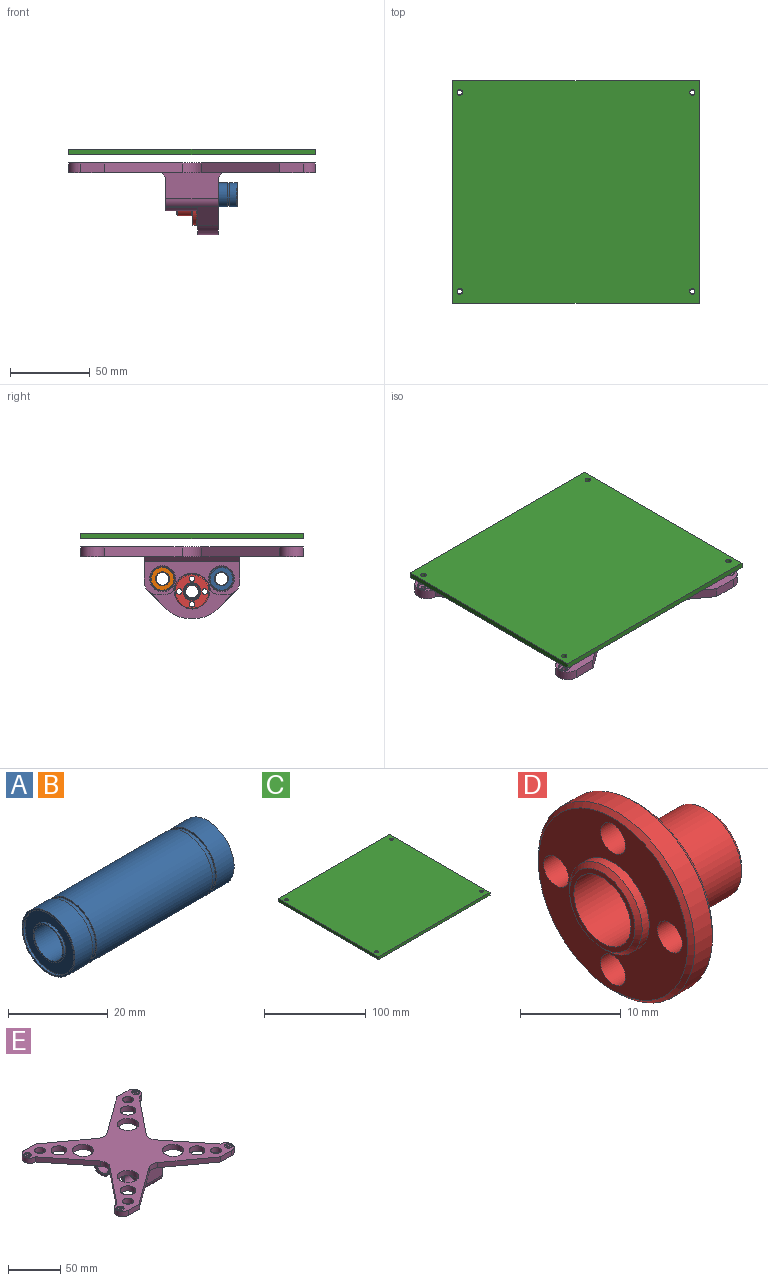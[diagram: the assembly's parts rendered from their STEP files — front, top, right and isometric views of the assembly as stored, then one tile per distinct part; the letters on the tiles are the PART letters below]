
ASSEMBLY  parts=5 mates=4
PART A: 20 faces, bbox 45x15x15 mm
  f0: plane 8.7x8.7mm, normal (-1,0,0), area 9.2mm2, adj f4,f17
  f1: plane 8.7x8.7mm, normal (1,0,0), area 9.2mm2, adj f4,f14
  f2: cylinder r=7.5mm len=32.8mm, axis (-1,0,0), area 1545.7mm2, adj f8,f11
  f3: cylinder r=7.5mm len=15mm, axis (-1,0,0), area 235.6mm2, adj f7,f9
  f4: cylinder r=4mm len=45mm, axis (-1,0,0), area 1131mm2, adj f0,f1
  f5: cylinder r=7.5mm len=15mm, axis (-1,0,0), area 235.6mm2, adj f6,f12
  f6: plane 15x15mm, normal (1,0,0), area 16.1mm2, adj f5,f15
  f7: plane 15x15mm, normal (-1,0,0), area 16.1mm2, adj f3,f18
  f8: plane 15x15mm, normal (-1,0,0), area 16.1mm2, adj f2,f10
  f9: plane 15x15mm, normal (1,0,0), area 16.1mm2, adj f3,f10
  f10: cylinder r=7.15mm len=14.3mm, axis (-1,0,0), area 49.4mm2, adj f8,f9
  f11: plane 15x15mm, normal (1,0,0), area 16.1mm2, adj f2,f13
  f12: plane 15x15mm, normal (-1,0,0), area 16.1mm2, adj f5,f13
  f13: cylinder r=7.15mm len=14.3mm, axis (1,0,0), area 49.4mm2, adj f11,f12
  f14: cylinder r=4.35mm len=8.7mm, axis (1,0,0), area 13.7mm2, adj f1,f16
  f15: cylinder r=7.15mm len=14.3mm, axis (1,0,0), area 22.5mm2, adj f6,f16
  f16: plane 14.3x14.3mm, normal (1,0,0), area 101.2mm2, adj f14,f15
  f17: cylinder r=4.35mm len=8.7mm, axis (-1,0,0), area 13.7mm2, adj f0,f19
  f18: cylinder r=7.15mm len=14.3mm, axis (-1,0,0), area 22.5mm2, adj f7,f19
  f19: plane 14.3x14.3mm, normal (-1,0,0), area 101.2mm2, adj f17,f18
PART B: same geometry as A
PART C: 10 faces, bbox 155x140x3.5 mm
  f0: plane 155x140mm, normal (0,0,1), area 21661.5mm2, adj f2,f3,f4,f5,f6,f7,f8,f9
  f1: plane 155x140mm, normal (0,0,-1), area 21661.5mm2, adj f2,f3,f4,f5,f6,f7,f8,f9
  f2: plane 140x3.5mm, normal (1,0,0), area 490mm2, adj f0,f1,f3,f5
  f3: plane 155x3.5mm, normal (0,1,0), area 542.5mm2, adj f0,f1,f2,f4
  f4: plane 140x3.5mm, normal (-1,0,0), area 490mm2, adj f0,f1,f3,f5
  f5: plane 155x3.5mm, normal (0,-1,0), area 542.5mm2, adj f0,f1,f2,f4
  f6: cylinder r=1.75mm len=3.5mm, axis (0,0,1), area 38.5mm2, adj f0,f1
  f7: cylinder r=1.75mm len=3.5mm, axis (0,0,1), area 38.5mm2, adj f0,f1
  f8: cylinder r=1.75mm len=3.5mm, axis (0,0,1), area 38.5mm2, adj f0,f1
  f9: cylinder r=1.75mm len=3.5mm, axis (0,0,1), area 38.5mm2, adj f0,f1
PART D: 17 faces, bbox 15x22x22 mm
  f0: cylinder r=11mm len=22mm, axis (-1,0,0), area 172.8mm2, adj f10,f11
  f1: plane 21x21mm, normal (1,0,0), area 209.4mm2, adj f8,f11,f13,f14,f15,f16
  f2: plane 21x21mm, normal (-1,0,0), area 226.2mm2, adj f6,f10,f13,f14,f15,f16
  f3: cylinder r=5.1mm len=10.2mm, axis (-1,0,0), area 288.4mm2, adj f8,f12
  f4: plane 9.2x9.2mm, normal (1,0,0), area 16.2mm2, adj f5,f12
  f5: cylinder r=4mm len=15mm, axis (1,0,0), area 377mm2, adj f4,f7
  f6: cylinder r=5.1mm len=10.2mm, axis (1,0,0), area 32mm2, adj f2,f9
  f7: plane 9.2x9.2mm, normal (-1,0,0), area 16.2mm2, adj f5,f9
  f8: cone r=5.1mm half-angle=45deg, axis (-1,0,0), area 23.8mm2, adj f1,f3
  f9: cone r=4.6mm half-angle=45deg, axis (1,0,0), area 21.5mm2, adj f6,f7
  f10: cone r=11mm half-angle=45deg, axis (1,0,0), area 47.8mm2, adj f0,f2
  f11: cone r=10.5mm half-angle=45deg, axis (-1,0,0), area 47.8mm2, adj f0,f1
  f12: cone r=4.6mm half-angle=45deg, axis (-1,0,0), area 21.5mm2, adj f3,f4
  f13: cylinder r=1.75mm len=3.5mm, axis (1,0,0), area 38.5mm2, adj f1,f2
  f14: cylinder r=1.75mm len=3.5mm, axis (1,0,0), area 38.5mm2, adj f1,f2
  f15: cylinder r=1.75mm len=3.5mm, axis (1,0,0), area 38.5mm2, adj f1,f2
  f16: cylinder r=1.75mm len=3.5mm, axis (1,0,0), area 38.5mm2, adj f1,f2
PART E: 83 faces, bbox 155x140x45 mm
  f0: plane 60x21.18mm, normal (-1,0,0), area 548.7mm2, adj f1,f2,f5,f6,f19,f20,f21,f25
  f1: plane 38.8x16.1mm, normal (0,-1,0), area 537.1mm2, adj f0,f3,f34,f35,f81,f82
  f2: plane 38.8x16.1mm, normal (0,1,0), area 537.1mm2, adj f0,f3,f33,f35,f81,f82
  f3: plane 60x36mm, normal (1,0,0), area 1172.9mm2, adj f1,f2,f4,f5,f6,f7,f8,f14
  f4: plane 12.8x3.43mm, normal (0,0,-1), area 43.9mm2, adj f3,f7,f8,f13
  f5: plane 32.8x12.09mm, normal (0,-0.71,-0.71), area 249.2mm2, adj f0,f3,f7,f13,f32,f34
  f6: plane 32.8x12.09mm, normal (0,0.71,-0.71), area 249.1mm2, adj f0,f3,f8,f13,f31,f33
  f7: cylinder r=20mm len=14.14mm, axis (1,0,0), area 201.1mm2, adj f3,f4,f5,f13
  f8: cylinder r=20mm len=14.14mm, axis (1,0,0), area 201.1mm2, adj f3,f4,f6,f13
  f9: cylinder r=7.68mm len=31.8mm, axis (1,0,0), area 1533.5mm2, adj f20,f23
  f10: cylinder r=5.4mm len=11.8mm, axis (1,0,0), area 400.4mm2, adj f18,f24
  f11: cylinder r=7.68mm len=31.8mm, axis (1,0,0), area 1533.5mm2, adj f21,f22
  f12: cylinder r=11mm len=21.11mm, axis (-1,0,0), area 551.3mm2, adj f13,f19,f29,f30
  f13: plane 53.76x28mm, normal (-1,0,0), area 608.4mm2, adj f4,f5,f6,f7,f8,f12,f14,f15
  f14: cylinder r=1.75mm len=12.8mm, axis (-1,0,0), area 140.7mm2, adj f3,f13
  f15: cylinder r=1.75mm len=12.8mm, axis (-1,0,0), area 140.7mm2, adj f3,f13
  f16: cylinder r=1.75mm len=12.8mm, axis (-1,0,0), area 140.7mm2, adj f3,f13
  f17: cylinder r=1.75mm len=12.8mm, axis (-1,0,0), area 140.7mm2, adj f3,f13
  f18: cone r=5.4mm half-angle=45deg, axis (-1,0,0), area 25.1mm2, adj f10,f13
  f19: cone r=11mm half-angle=45deg, axis (-1,0,0), area 22.4mm2, adj f0,f12,f29,f30
  f20: cone r=7.68mm half-angle=45deg, axis (-1,0,0), area 35.2mm2, adj f0,f9
  f21: cone r=7.68mm half-angle=45deg, axis (-1,0,0), area 35.2mm2, adj f0,f11
  f22: cone r=7.68mm half-angle=45deg, axis (1,0,0), area 35.2mm2, adj f3,f11
  f23: cone r=7.68mm half-angle=45deg, axis (1,0,0), area 35.2mm2, adj f3,f9
  f24: cone r=5.4mm half-angle=45deg, axis (1,0,0), area 25.1mm2, adj f3,f10
  f25: cylinder r=10.18mm len=20mm, axis (-1,0,0), area 89mm2, adj f0,f13,f26,f30
  f26: plane 20x3.03mm, normal (0,0,-1), area 60.6mm2, adj f0,f13,f25,f31
  f27: cylinder r=10.18mm len=20mm, axis (-1,0,0), area 85.3mm2, adj f0,f13,f28,f29
  f28: plane 20x3.21mm, normal (0,0,-1), area 64.2mm2, adj f0,f13,f27,f32
  f29: cylinder r=7mm len=20mm, axis (1,0,0), area 123.5mm2, adj f0,f12,f13,f19,f27
  f30: cylinder r=7mm len=20mm, axis (1,0,0), area 123.5mm2, adj f0,f12,f13,f19,f25
  f31: cylinder r=7mm len=20mm, axis (-1,0,0), area 110mm2, adj f0,f6,f13,f26
  f32: cylinder r=7mm len=20mm, axis (-1,0,0), area 110mm2, adj f0,f5,f13,f28
  f33: cylinder r=7mm len=32.8mm, axis (-1,0,0), area 180.3mm2, adj f0,f2,f3,f6
  f34: cylinder r=7mm len=32.8mm, axis (1,0,0), area 180.3mm2, adj f0,f1,f3,f5
  f35: plane 155x140mm, normal (0,0,-1), area 6124.2mm2, adj f1,f2,f37,f40,f43,f46,f48,f49
  f36: plane 7.5x7.5mm, normal (0,0,1), area 37.1mm2, adj f37,f38
  f37: cylinder r=1.5mm len=4.5mm, axis (0,0,1), area 42.4mm2, adj f35,f36
  f38: cylinder r=3.75mm len=7.5mm, axis (0,0,1), area 35.3mm2, adj f36,f79
  f39: plane 7.5x7.5mm, normal (0,0,1), area 37.1mm2, adj f40,f41
  f40: cylinder r=1.5mm len=4.5mm, axis (0,0,1), area 42.4mm2, adj f35,f39
  f41: cylinder r=3.75mm len=7.5mm, axis (0,0,1), area 35.3mm2, adj f39,f79
  f42: plane 7.5x7.5mm, normal (0,0,1), area 37.1mm2, adj f43,f44
  f43: cylinder r=1.5mm len=4.5mm, axis (0,0,1), area 42.4mm2, adj f35,f42
  f44: cylinder r=3.75mm len=7.5mm, axis (0,0,1), area 35.3mm2, adj f42,f79
  f45: plane 7.5x7.5mm, normal (0,0,1), area 37.1mm2, adj f46,f47
  f46: cylinder r=1.5mm len=4.5mm, axis (0,0,1), area 42.4mm2, adj f35,f45
  f47: cylinder r=3.75mm len=7.5mm, axis (0,0,1), area 35.3mm2, adj f45,f79
  f48: cylinder r=5mm len=10mm, axis (0,0,-1), area 188.5mm2, adj f35,f79
  f49: cylinder r=10mm len=20mm, axis (0,0,-1), area 377mm2, adj f35,f79
  f50: cylinder r=7.5mm len=15mm, axis (0,0,-1), area 282.7mm2, adj f35,f79
  f51: cylinder r=10mm len=20mm, axis (0,0,-1), area 377mm2, adj f35,f79
  f52: cylinder r=7.5mm len=15mm, axis (0,0,-1), area 282.7mm2, adj f35,f79
  f53: cylinder r=7.5mm len=15mm, axis (0,0,1), area 141.4mm2, adj f35,f54,f72,f79
  f54: plane 15x6mm, normal (0,-1,0), area 90mm2, adj f35,f53,f55,f79
  f55: plane 49.12x35.72mm, normal (0.59,-0.81,0), area 364.4mm2, adj f35,f54,f56,f79
  f56: cylinder r=10mm len=11.76mm, axis (0,0,1), area 75.5mm2, adj f35,f55,f57,f79
  f57: plane 49.12x35.72mm, normal (-0.59,-0.81,0), area 364.4mm2, adj f35,f56,f58,f79
  f58: plane 15x6mm, normal (0,-1,0), area 90mm2, adj f35,f57,f59,f79
  f59: cylinder r=7.5mm len=15mm, axis (0,0,1), area 141.4mm2, adj f35,f58,f60,f79
  f60: plane 48.75x39mm, normal (0.78,0.62,0), area 374.6mm2, adj f35,f59,f61,f79
  f61: cylinder r=10mm len=12.49mm, axis (0,0,1), area 81mm2, adj f35,f60,f62,f79
  f62: plane 48.75x39mm, normal (0.78,-0.62,0), area 374.6mm2, adj f35,f61,f63,f79
  f63: cylinder r=7.5mm len=15mm, axis (0,0,1), area 141.4mm2, adj f35,f62,f64,f79
  f64: plane 15x6mm, normal (0,1,0), area 90mm2, adj f35,f63,f65,f79
  f65: plane 49.12x35.72mm, normal (-0.59,0.81,0), area 364.4mm2, adj f35,f64,f66,f79
  f66: cylinder r=10mm len=11.76mm, axis (0,0,1), area 75.5mm2, adj f35,f65,f67,f79
  f67: plane 49.12x35.72mm, normal (0.59,0.81,0), area 364.4mm2, adj f35,f66,f68,f79
  f68: plane 15x6mm, normal (0,1,0), area 90mm2, adj f35,f67,f69,f79
  f69: cylinder r=7.5mm len=15mm, axis (0,0,1), area 141.4mm2, adj f35,f68,f70,f79
  f70: plane 48.75x39mm, normal (-0.78,-0.62,0), area 374.6mm2, adj f35,f69,f71,f79
  f71: cylinder r=10mm len=12.49mm, axis (0,0,1), area 81mm2, adj f35,f70,f72,f79
  f72: plane 48.75x39mm, normal (-0.78,0.62,0), area 374.6mm2, adj f35,f53,f71,f79
  f73: cylinder r=10mm len=20mm, axis (0,0,-1), area 377mm2, adj f35,f79
  f74: cylinder r=10mm len=20mm, axis (0,0,-1), area 377mm2, adj f35,f79
  f75: cylinder r=7.5mm len=15mm, axis (0,0,-1), area 282.7mm2, adj f35,f79
  f76: cylinder r=5mm len=10mm, axis (0,0,-1), area 188.5mm2, adj f35,f79
  f77: cylinder r=7.5mm len=15mm, axis (0,0,-1), area 282.7mm2, adj f35,f79
  f78: cylinder r=5mm len=10mm, axis (0,0,-1), area 188.5mm2, adj f35,f79
  f79: plane 155x140mm, normal (0,0,1), area 8303.8mm2, adj f38,f41,f44,f47,f48,f49,f50,f51
  f80: cylinder r=5mm len=10mm, axis (0,0,-1), area 188.5mm2, adj f35,f79
  f81: plane 60x3mm, normal (0.71,0,-0.71), area 254.6mm2, adj f1,f2,f3,f35
  f82: plane 60x3mm, normal (-0.71,0,-0.71), area 254.6mm2, adj f0,f1,f2,f35
PLACE A rot(axis=(0,1,0),180deg) t=(6.1,-18.5,25)mm
PLACE B t=(6.1,18.5,25)mm
PLACE C t=(0,0,50)mm
PLACE D rot(axis=(0,0,-1),180deg) t=(3.6,0,17)mm
PLACE E at identity fixed
MATE fastened A.f2 <-> E.f9  axis (-1,0,0) through (-16.4,-18.5,25)mm
MATE fastened C.f6 <-> E.f37  axis (0,0,-1) through (-73,62.5,50)mm
MATE fastened E.f21 <-> B.f2  axis (-1,0,0) through (-16.4,18.5,25)mm
MATE fastened D.f16 <-> E.f14  axis (1,0,0) through (3.6,0,25)mm
